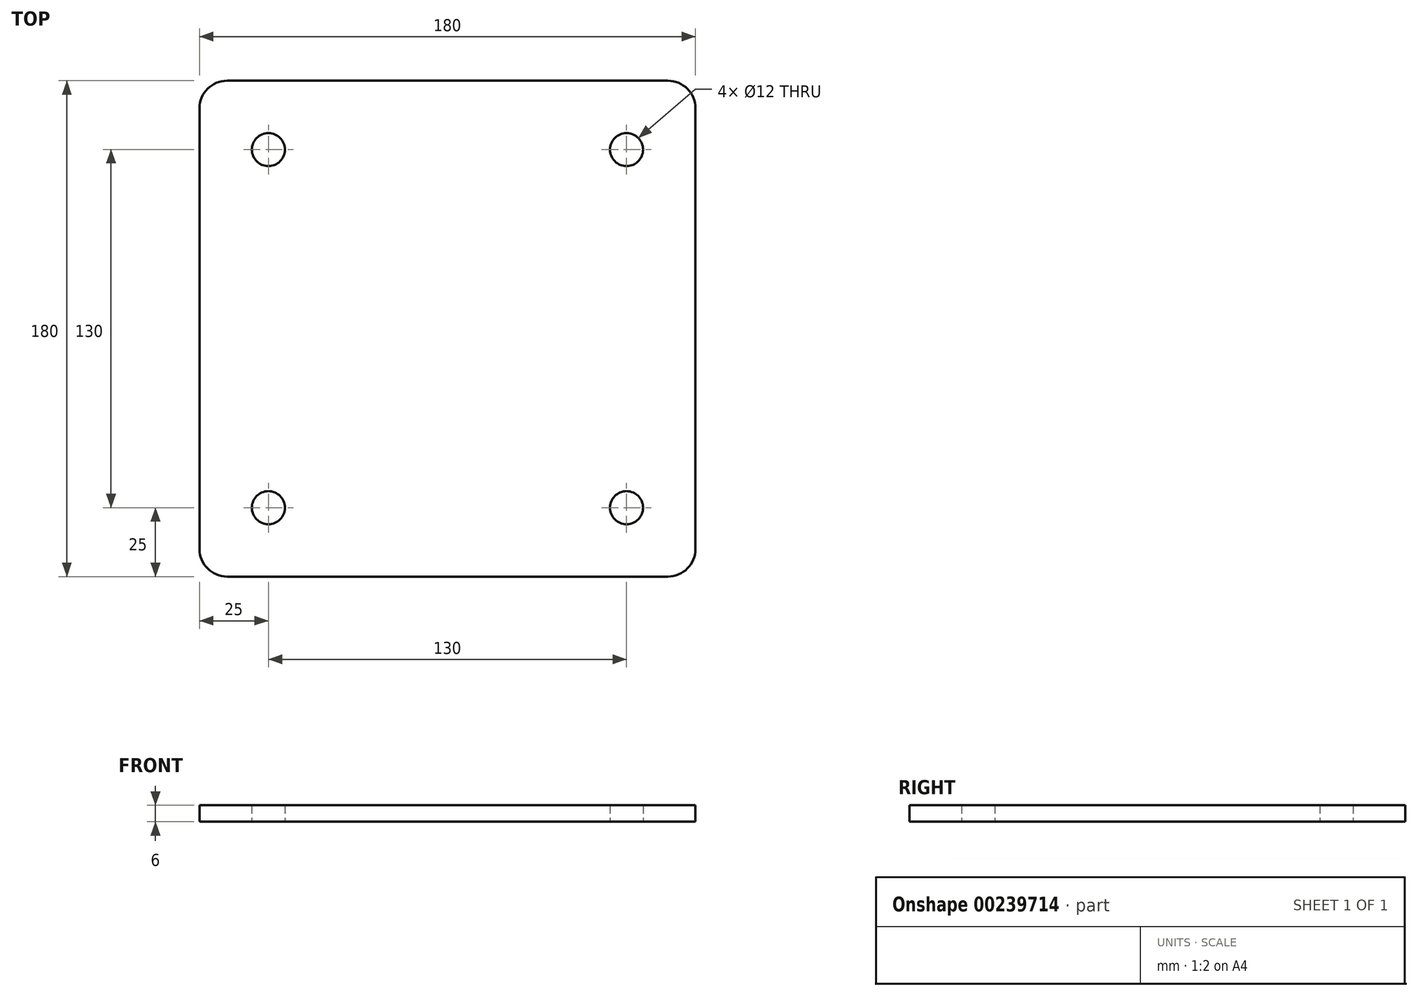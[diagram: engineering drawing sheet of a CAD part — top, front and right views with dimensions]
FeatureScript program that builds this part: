
annotation { "Feature Type Name" : "Feature", "Feature Type Description" : "" }
export const myFeature = defineFeature(function(context is Context, id is Id, definition is map)
    precondition{}
    {
        {
            var Q0;
            Q0=qCreatedBy(makeId("Top.planeOp"),FACE);
            var sketch = newSketch(context, id + "F0", { "sketchPlane" : qUnion([Q0])});
            skLineSegment(sketch, "E0.bottom", {"start": v(80, 90) * mm, "end": v(-80, 90) * mm});
            skLineSegment(sketch, "E0.top", {"start": v(80, -90) * mm, "end": v(-80, -90) * mm});
            skLineSegment(sketch, "E0.left", {"start": v(90, 80) * mm, "end": v(90, -80) * mm});
            skLineSegment(sketch, "E0.right", {"start": v(-90, 80) * mm, "end": v(-90, -80) * mm});
            skPoint(sketch, "E0.middle", {"position": v(0, 0) * mm});
            skPoint(sketch, "E1.visualSharp", {"position": v(-90, 90) * mm});
            skArc(sketch, "E1.filletArc", {"start": v(-80, 90) * mm, "mid": v(-87.07, 87.07) * mm, "end": v(-90, 80) * mm});
            skPoint(sketch, "E2.visualSharp", {"position": v(90, 90) * mm});
            skArc(sketch, "E2.filletArc", {"start": v(90, 80) * mm, "mid": v(87.07, 87.07) * mm, "end": v(80, 90) * mm});
            skPoint(sketch, "E3.visualSharp", {"position": v(90, -90) * mm});
            skArc(sketch, "E3.filletArc", {"start": v(80, -90) * mm, "mid": v(87.07, -87.07) * mm, "end": v(90, -80) * mm});
            skPoint(sketch, "E4.visualSharp", {"position": v(-90, -90) * mm});
            skArc(sketch, "E4.filletArc", {"start": v(-90, -80) * mm, "mid": v(-87.07, -87.07) * mm, "end": v(-80, -90) * mm});
            skCircle(sketch, "E5", {"center": v(-65, 65) * mm, "radius": 6 * mm});
            skCircle(sketch, "E6.0.1.0", {"center": v(-65, -65) * mm, "radius": 6 * mm});
            skCircle(sketch, "E6.1.0.0", {"center": v(65, 65) * mm, "radius": 6 * mm});
            skCircle(sketch, "E6.1.1.0", {"center": v(65, -65) * mm, "radius": 6 * mm});
            skLineSegment(sketch, "E6.direction1", {"start": v(-65, 65) * mm, "end": v(65, 65) * mm, "construction": true});
            skLineSegment(sketch, "E6.direction2", {"start": v(-65, 65) * mm, "end": v(-65, -65) * mm, "construction": true});
            skSolve(sketch);
        }
        {
            var Q0;
            Q0=makeQuery(id+"F0.imprint","IMPRINT",FACE,{"disambiguationData":[TD([[makeQuery(id+"F0.imprint","IMPRINT",EDGE,{"derivedFrom":sQuery(id+"F0.wireOp",EDGE,"E0.bottom")}),1.0]])]});
            extrude(context, id + "F1", {"entities" : qUnion([Q0]), "depth" : 6 * mm});
        }
    });
